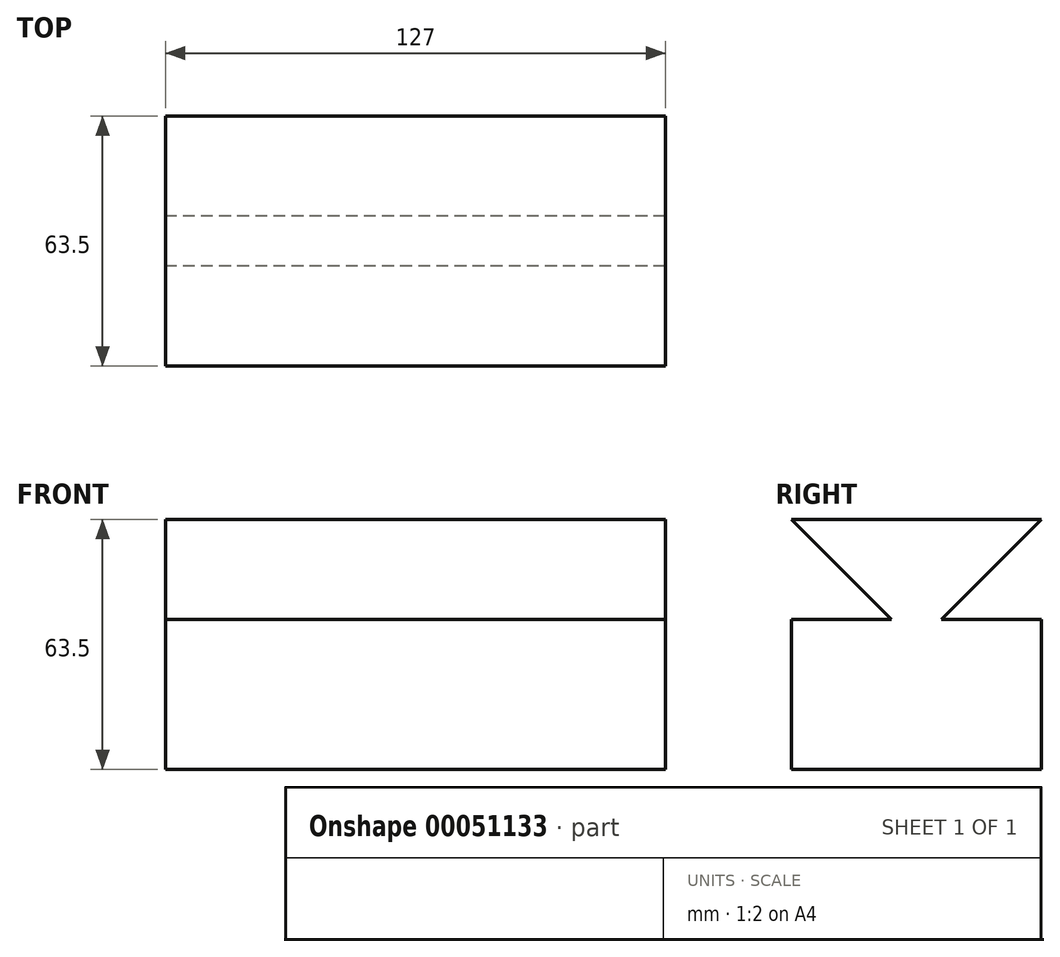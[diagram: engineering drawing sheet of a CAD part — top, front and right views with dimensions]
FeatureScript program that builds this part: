
annotation { "Feature Type Name" : "Feature", "Feature Type Description" : "" }
export const myFeature = defineFeature(function(context is Context, id is Id, definition is map)
    precondition{}
    {
        {
            var Q0;
            Q0=qCreatedBy(makeId("Right.planeOp"),FACE);
            var sketch = newSketch(context, id + "F0", { "sketchPlane" : qUnion([Q0])});
            skLineSegment(sketch, "E0.rect.bottom", {"start": v(31.75, 31.75) * mm, "end": v(-31.75, 31.75) * mm});
            skLineSegment(sketch, "E0.rect.top", {"start": v(31.75, -31.75) * mm, "end": v(-31.75, -31.75) * mm});
            skLineSegment(sketch, "E0.rect.left", {"start": v(31.75, 6.35) * mm, "end": v(31.75, -31.75) * mm});
            skLineSegment(sketch, "E0.rect.right", {"start": v(-31.75, 6.35) * mm, "end": v(-31.75, -31.75) * mm});
            skPoint(sketch, "E0.rect.middle", {"position": v(0, 0) * mm});
            skLineSegment(sketch, "E1", {"start": v(-31.75, 6.35) * mm, "end": v(-6.35, 6.35) * mm});
            skLineSegment(sketch, "E2", {"start": v(-31.75, 31.75) * mm, "end": v(-6.35, 6.35) * mm});
            skLineSegment(sketch, "E3", {"start": v(31.75, 31.75) * mm, "end": v(6.35, 6.35) * mm});
            skLineSegment(sketch, "E4.trimOffspring", {"start": v(6.35, 6.35) * mm, "end": v(31.75, 6.35) * mm});
            skSolve(sketch);
        }
        {
            var Q0;
            Q0 = qSketchRegion(id + "F0", true);
            extrude(context, id + "F1", {"entities" : qUnion([Q0]), "depth" : 101.6 * mm});
        }
        {
            var Q0;
            Q0 = qSketchRegion(id + "F0", true);
            extrude(context, id + "F2", {"entities" : qUnion([Q0]), "operationType" : NewBodyOperationType.ADD, "depth" : 127 * mm});
        }
    });
